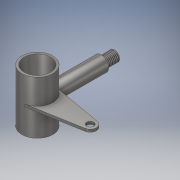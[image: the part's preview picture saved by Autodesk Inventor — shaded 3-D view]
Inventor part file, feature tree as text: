
AUTODESK INVENTOR PART (.ipt)
format: ipt  version: 2019 (Build 230136000, 136)  size: 185,856 bytes
history: native  units: mm
features: extrude x5, plane x3, sketch x3, thread x1, projected_geometry x1
ambient origin geometry x8: Origin, YZ Plane, XZ Plane, XY Plane, X Axis, Y Axis, Z Axis, Center Point
bodies: Solid1 (feature_tree)
feature tree (13):
  extrude  "Extrusion1"  Depth=30.0mm
  plane  "Work Plane5"
  plane  "Work Plane6"
  extrude  "Extrusion5"  Depth=9.599311mm
  plane  "Work Plane7"
  sketch  "Sketch8"  dims[d35=14.0mm d36=60.0mm d37=8.0mm d38=3.0mm d39=0.0mm d40=55.0mm d41=0.0mm d42=70.0mm d43=0.0mm d44=70.0mm d45=0.0mm d46=10.0mm d47=0.0mm]
  extrude  "Extrusion6"  Depth=10.0mm
  extrude  "Extrusion7"  Depth=10.0mm
  extrude  "Extrusion8"  Depth=10.0mm TaperAngle=0.0deg
  thread  "Thread2"  [1 undecoded]
  sketch  "Sketch1"  dims[d0=35.0mm d1=30.0mm]
  sketch  "Sketch7"  dims[d2=60.0mm d3=0.0mm d23=9.599311mm]
  projected_geometry  "Projected Loop4"
note: 1 required parameter value undecoded (feature->parameter linkage not recoverable at this tier; creation-order binding heuristic only, values carry confidence <= 0.55)
